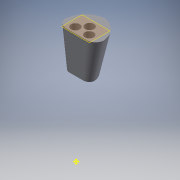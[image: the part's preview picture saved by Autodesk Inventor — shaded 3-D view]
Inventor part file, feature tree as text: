
AUTODESK INVENTOR PART (.ipt)
format: ipt  version: 2018 (Build 220112000, 112)  size: 186,880 bytes
history: native  units: mm
features: sketch x4, reference x4, other x3, extrude x2, plane x1, loft x1
ambient origin geometry x8: Origin, YZ Plane, XZ Plane, XY Plane, X Axis, Y Axis, Z Axis, Center Point
bodies: Solid1 (feature_tree)
feature tree (15):
  sketch  "Sketch1"  dims[d0=0.0mm d1=90.0deg d2=0.0mm d3=90.0deg]
  plane  "Work Plane1"
  loft  "Loft1"
  extrude  "Extrusion1"  Depth=6.0mm
  extrude  "Extrusion2"  Depth=20.0mm TaperAngle=0.0deg
  other  "Work Point1"
  reference  "Reference1"
  sketch  "Sketch2"  dims[d4=6.0mm d5=6.0mm]
  sketch  "Sketch3"  dims[d6=6.0mm d7=20.0mm d8=0.0mm]
  reference  "Reference3"
  reference  "Reference4"
  reference  "Reference5"
  sketch  "Sketch4"  dims[d9=3.0mm d10=3.0mm d11=3.0mm d12=20.0mm d13=0.0mm]
  other  "TailAssembly.iam"
  other  "Tail6:1"
